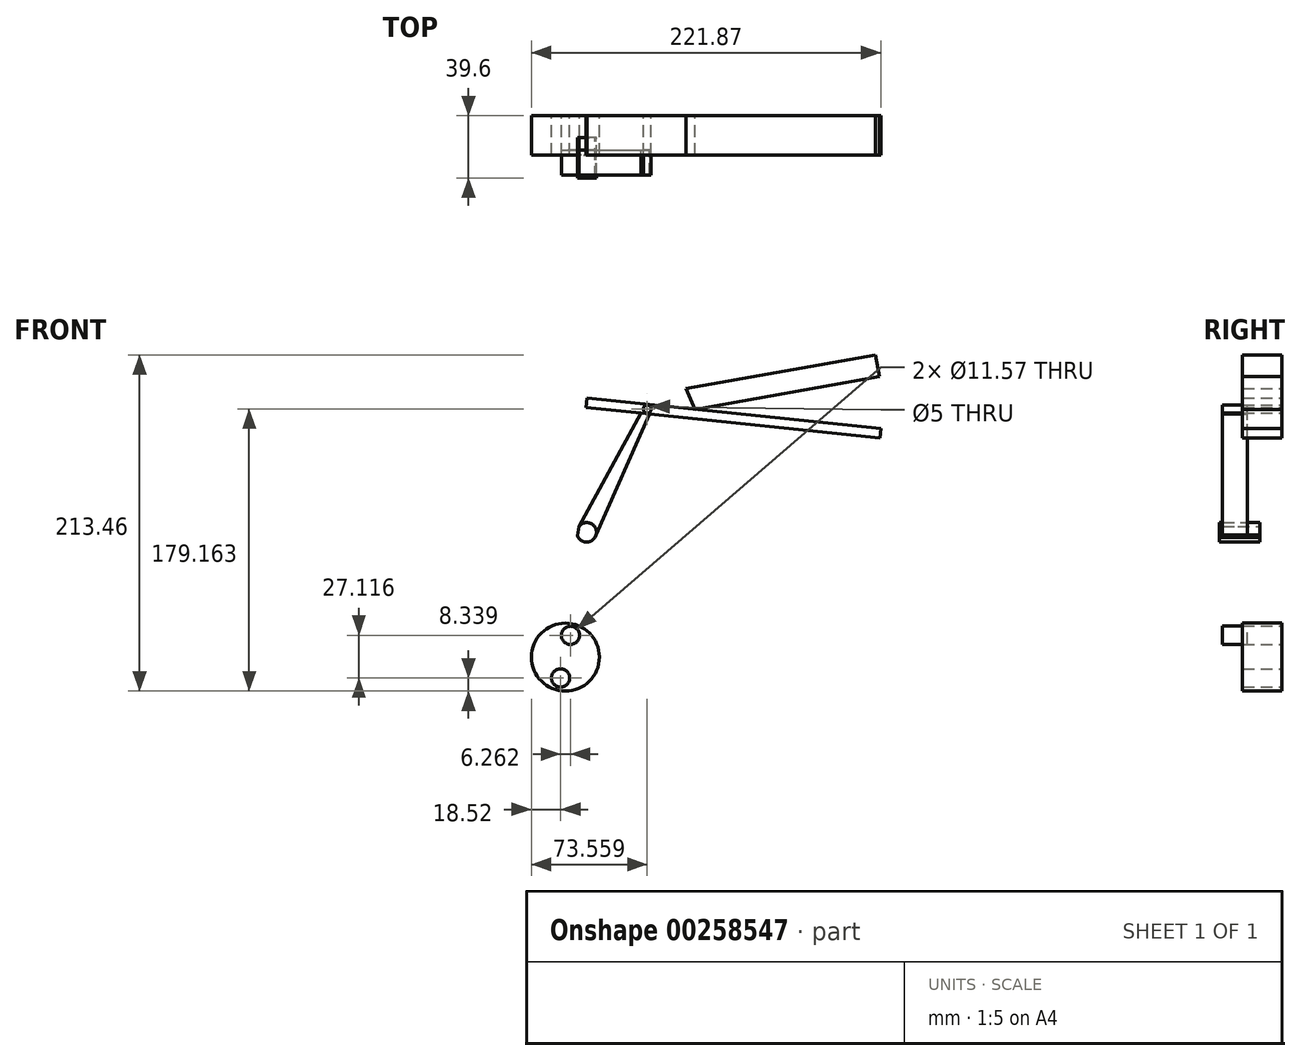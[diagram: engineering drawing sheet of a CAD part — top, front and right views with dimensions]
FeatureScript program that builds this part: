
annotation { "Feature Type Name" : "Feature", "Feature Type Description" : "" }
export const myFeature = defineFeature(function(context is Context, id is Id, definition is map)
    precondition{}
    {
        {
            var Q0;
            Q0=qCreatedBy(makeId("Front.planeOp"),FACE);
            var sketch = newSketch(context, id + "F0", { "sketchPlane" : qUnion([Q0])});
            skCircle(sketch, "E0", {"center": v(-26.33, -38.77) * mm, "radius": 21.58 * mm});
            skLineSegment(sketch, "E1", {"start": v(-31.19, -59.8) * mm, "end": v(-21.48, -17.74) * mm});
            skCircle(sketch, "E2", {"center": v(-23.13, -24.9) * mm, "radius": 5.79 * mm});
            skCircle(sketch, "E3", {"center": v(-29.4, -52.01) * mm, "radius": 5.79 * mm});
            skCircle(sketch, "E4", {"center": v(-12.8, 40.5) * mm, "radius": 6.2 * mm});
            skLineSegment(sketch, "E5", {"start": v(-13.2, 119.83) * mm, "end": v(173.34, 100.46) * mm});
            skLineSegment(sketch, "E6", {"start": v(173.96, 106.43) * mm, "end": v(173.34, 100.46) * mm});
            skLineSegment(sketch, "E7", {"start": v(173.96, 106.43) * mm, "end": v(-12.58, 125.8) * mm});
            skLineSegment(sketch, "E8", {"start": v(-12.58, 125.8) * mm, "end": v(-13.2, 119.83) * mm});
            skLineSegment(sketch, "E9", {"start": v(25.34, 115.83) * mm, "end": v(25.96, 121.8) * mm, "construction": true});
            skPoint(sketch, "E10", {"position": v(25.65, 118.81) * mm});
            skCircle(sketch, "E11", {"center": v(25.65, 118.81) * mm, "radius": 2.5 * mm});
            skLineSegment(sketch, "E12", {"start": v(-17.72, 44.29) * mm, "end": v(23.15, 118.81) * mm});
            skLineSegment(sketch, "E13", {"start": v(-7.54, 37.22) * mm, "end": v(27.94, 117.8) * mm});
            skLineSegment(sketch, "E14", {"start": v(-17.34, -24.92) * mm, "end": v(-7.54, 37.22) * mm});
            skLineSegment(sketch, "E15", {"start": v(-17.72, 44.29) * mm, "end": v(-28.84, -23.96) * mm});
            skLineSegment(sketch, "E16", {"start": v(50.14, 131.76) * mm, "end": v(170.6, 153.11) * mm});
            skLineSegment(sketch, "E17", {"start": v(170.6, 153.11) * mm, "end": v(173.02, 139.4) * mm});
            skLineSegment(sketch, "E18", {"start": v(173.02, 139.4) * mm, "end": v(56.07, 118.67) * mm});
            skLineSegment(sketch, "E19", {"start": v(56.07, 118.67) * mm, "end": v(50.14, 131.76) * mm});
            skLineSegment(sketch, "E20", {"start": v(20.2, 116.36) * mm, "end": v(29.83, 115.36) * mm});
            skSolve(sketch);
        }
        {
            var Q0;
            {var subQ3=sQuery(id+"F0.wireOp",EDGE,"E1");var subQ5=sQuery(id+"F0.wireOp",EDGE,"E0");var subQ10=makeQuery(id+"F0.imprint","INTERSECT",VERTEX,{"disambiguationData":[OD(0.0)],"derivedFrom":[subQ5,subQ3]});Q0=makeQuery(id+"F0.imprint","IMPRINT",FACE,{"disambiguationData":[TD([[makeQuery(id+"F0.imprint","IMPRINT",EDGE,{"disambiguationData":[TD([[subQ10,1.0]])],"derivedFrom":subQ5}),1.0]])]});}
            var Q1;
            {var subQ0=sQuery(id+"F0.wireOp",EDGE,"E1");var subQ1=sQuery(id+"F0.wireOp",EDGE,"E0");var subQ2=makeQuery(id+"F0.imprint","INTERSECT",VERTEX,{"disambiguationData":[OD(1.0)],"derivedFrom":[subQ1,subQ0]});Q1=makeQuery(id+"F0.imprint","IMPRINT",FACE,{"disambiguationData":[TD([[makeQuery(id+"F0.imprint","IMPRINT",EDGE,{"disambiguationData":[TD([[subQ2,-1.0]])],"derivedFrom":subQ1}),1.0]])]});}
            var Q2;
            {var subQ0=sQuery(id+"F0.wireOp",EDGE,"E1");var subQ1=sQuery(id+"F0.wireOp",EDGE,"E0");var subQ2=makeQuery(id+"F0.imprint","INTERSECT",VERTEX,{"disambiguationData":[OD(1.0)],"derivedFrom":[subQ1,subQ0]});Q2=makeQuery(id+"F0.imprint","IMPRINT",FACE,{"disambiguationData":[TD([[makeQuery(id+"F0.imprint","IMPRINT",EDGE,{"disambiguationData":[TD([[subQ2,1.0]])],"derivedFrom":subQ1}),1.0]])]});}
            var Q3;
            {var subQ3=sQuery(id+"F0.wireOp",EDGE,"E1");var subQ7=sQuery(id+"F0.wireOp",EDGE,"E0");var subQ9=makeQuery(id+"F0.imprint","INTERSECT",VERTEX,{"disambiguationData":[OD(0.0)],"derivedFrom":[subQ7,subQ3]});Q3=makeQuery(id+"F0.imprint","IMPRINT",FACE,{"disambiguationData":[TD([[makeQuery(id+"F0.imprint","IMPRINT",EDGE,{"disambiguationData":[TD([[subQ9,-1.0]])],"derivedFrom":subQ7}),1.0]])]});}
            var Q4;
            Q4=makeQuery(id+"F0.imprint","IMPRINT",FACE,{"disambiguationData":[TD([[makeQuery(id+"F0.imprint","IMPRINT",EDGE,{"derivedFrom":sQuery(id+"F0.wireOp",EDGE,"E16")}),-1.0]])]});
            extrude(context, id + "F1", {"entities" : qUnion([Q0, Q1, Q2, Q3, Q4]), "depth" : 25 * mm});
        }
        {
            var Q0;
            {var subQ11=sQuery(id+"F0.wireOp",EDGE,"E6");Q0=makeQuery(id+"F0.imprint","IMPRINT",FACE,{"disambiguationData":[TD([[makeQuery(id+"F0.imprint","IMPRINT",EDGE,{"derivedFrom":subQ11}),-1.0]])]});}
            var Q1;
            {var subQ0=sQuery(id+"F0.wireOp",EDGE,"E12");var subQ1=sQuery(id+"F0.wireOp",EDGE,"E11");var subQ2=makeQuery(id+"F0.imprint","INTERSECT",VERTEX,{"derivedFrom":[subQ1,subQ0]});Q1=makeQuery(id+"F0.imprint","IMPRINT",FACE,{"disambiguationData":[TD([[makeQuery(id+"F0.imprint","IMPRINT",EDGE,{"disambiguationData":[TD([[subQ2,-1.0]])],"derivedFrom":subQ1}),-1.0]])]});}
            extrude(context, id + "F2", {"entities" : qUnion([Q0, Q1]), "depth" : 25 * mm});
        }
        {
            var Q0;
            {var subQ0=sQuery(id+"F0.wireOp",EDGE,"E11");var subQ1=makeQuery(id+"F0.imprint","INTERSECT",VERTEX,{"derivedFrom":[subQ0,sQuery(id+"F0.wireOp",EDGE,"E12")]});Q0=makeQuery(id+"F0.imprint","IMPRINT",FACE,{"disambiguationData":[TD([[makeQuery(id+"F0.imprint","IMPRINT",EDGE,{"disambiguationData":[TD([[subQ1,-1.0]])],"derivedFrom":subQ0}),1.0]])]});}
            var Q1;
            {var subQ1=sQuery(id+"F0.wireOp",EDGE,"E4");var subQ3=sQuery(id+"F0.wireOp",EDGE,"E13");var subQ4=makeQuery(id+"F0.imprint","INTERSECT",VERTEX,{"derivedFrom":[subQ1,subQ3]});Q1=makeQuery(id+"F0.imprint","IMPRINT",FACE,{"disambiguationData":[TD([[makeQuery(id+"F0.imprint","IMPRINT",EDGE,{"disambiguationData":[TD([[subQ4,-1.0]])],"derivedFrom":subQ3}),1.0]])]});}
            var Q2;
            {var subQ3=sQuery(id+"F0.wireOp",EDGE,"E0");var subQ7=makeQuery(id+"F0.imprint","INTERSECT",VERTEX,{"disambiguationData":[OD(1.0)],"derivedFrom":[subQ3,sQuery(id+"F0.wireOp",EDGE,"E1")]});Q2=makeQuery(id+"F0.imprint","IMPRINT",FACE,{"disambiguationData":[TD([[makeQuery(id+"F0.imprint","IMPRINT",EDGE,{"disambiguationData":[TD([[subQ7,1.0]])],"derivedFrom":subQ3}),-1.0]])]});}
            var Q3;
            {var subQ0=sQuery(id+"F0.wireOp",EDGE,"E2");var subQ1=sQuery(id+"F0.wireOp",EDGE,"E1");var subQ2=makeQuery(id+"F0.imprint","INTERSECT",VERTEX,{"disambiguationData":[OD(0.0)],"derivedFrom":[subQ1,subQ0]});Q3=makeQuery(id+"F0.imprint","IMPRINT",FACE,{"disambiguationData":[TD([[makeQuery(id+"F0.imprint","IMPRINT",EDGE,{"disambiguationData":[TD([[subQ2,-1.0]])],"derivedFrom":subQ1}),-1.0]])]});}
            var Q4;
            {var subQ0=sQuery(id+"F0.wireOp",EDGE,"E2");var subQ1=sQuery(id+"F0.wireOp",EDGE,"E1");var subQ2=makeQuery(id+"F0.imprint","INTERSECT",VERTEX,{"disambiguationData":[OD(0.0)],"derivedFrom":[subQ1,subQ0]});Q4=makeQuery(id+"F0.imprint","IMPRINT",FACE,{"disambiguationData":[TD([[makeQuery(id+"F0.imprint","IMPRINT",EDGE,{"disambiguationData":[TD([[subQ2,-1.0]])],"derivedFrom":subQ1}),1.0]])]});}
            extrude(context, id + "F3", {"entities" : qUnion([Q0, Q1, Q2, Q3, Q4]), "depth" : 37.8 * mm, "hasSecondDirection" : true, "secondDirectionOppositeDirection" : false, "secondDirectionDepth" : 21.9 * mm});
        }
        {
            var Q0;
            {var subQ1=sQuery(id+"F0.wireOp",EDGE,"E4");var subQ3=sQuery(id+"F0.wireOp",EDGE,"E15");var subQ4=makeQuery(id+"F0.imprint","INTERSECT",VERTEX,{"derivedFrom":[subQ1,subQ3]});Q0=makeQuery(id+"F0.imprint","IMPRINT",FACE,{"disambiguationData":[TD([[makeQuery(id+"F0.imprint","IMPRINT",EDGE,{"disambiguationData":[TD([[subQ4,-1.0]])],"derivedFrom":subQ1}),1.0]])]});}
            extrude(context, id + "F4", {"entities" : qUnion([Q0]), "depth" : 39.6 * mm, "hasSecondDirection" : true, "secondDirectionOppositeDirection" : false, "secondDirectionDepth" : 14.1 * mm});
        }
    });
